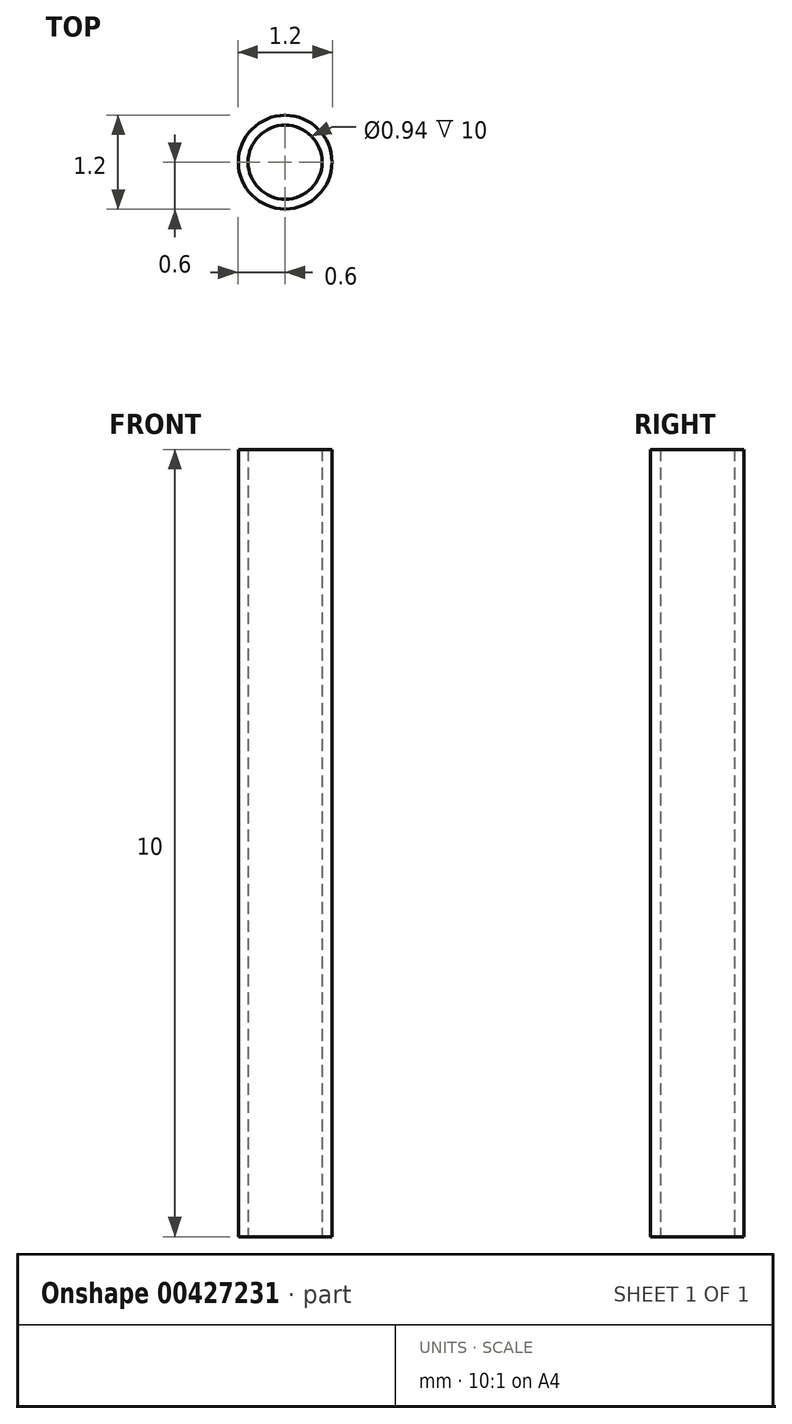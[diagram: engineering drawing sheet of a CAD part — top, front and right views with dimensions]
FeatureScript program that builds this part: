
annotation { "Feature Type Name" : "Feature", "Feature Type Description" : "" }
export const myFeature = defineFeature(function(context is Context, id is Id, definition is map)
    precondition{}
    {
        {
            var Q0;
            Q0=qCreatedBy(makeId("Top.planeOp"),FACE);
            var sketch = newSketch(context, id + "F0", { "sketchPlane" : qUnion([Q0])});
            skCircle(sketch, "E0", {"center": v(0, 0) * mm, "radius": 0.6 * mm});
            skCircle(sketch, "E1", {"center": v(0, 0) * mm, "radius": 0.47 * mm});
            skSolve(sketch);
        }
        {
            var Q0;
            Q0=makeQuery(id+"F0.imprint","IMPRINT",FACE,{"disambiguationData":[TD([[makeQuery(id+"F0.imprint","IMPRINT",EDGE,{"derivedFrom":sQuery(id+"F0.wireOp",EDGE,"E0")}),1.0]])]});
            extrude(context, id + "F1", {"entities" : qUnion([Q0]), "depth" : 10 * mm});
        }
    });
